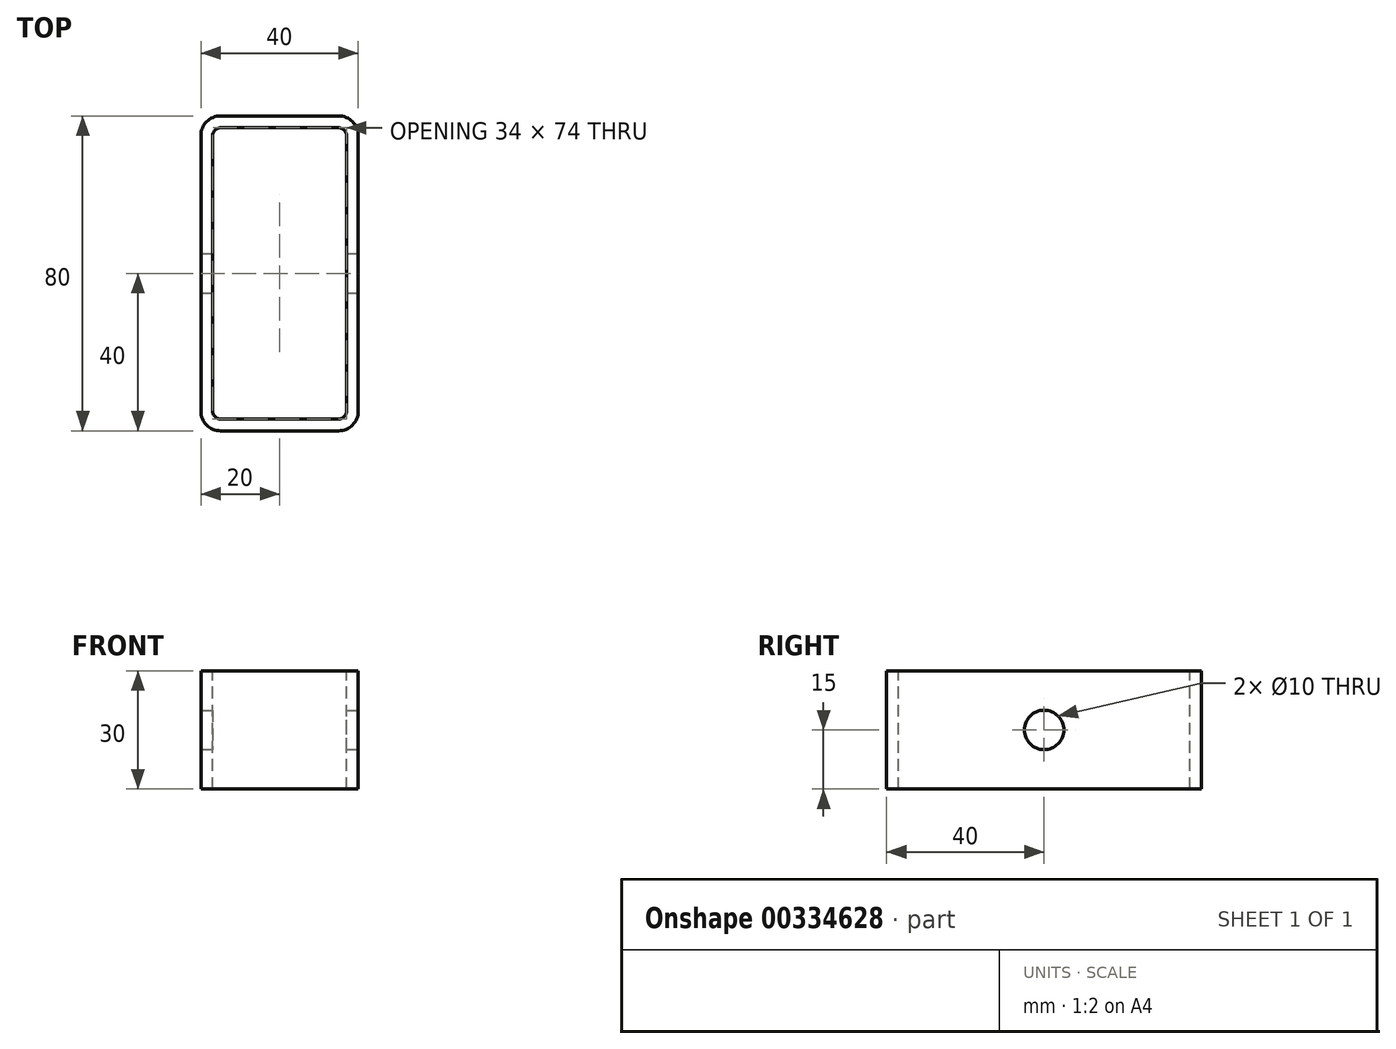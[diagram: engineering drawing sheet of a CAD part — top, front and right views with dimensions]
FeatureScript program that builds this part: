
annotation { "Feature Type Name" : "Feature", "Feature Type Description" : "" }
export const myFeature = defineFeature(function(context is Context, id is Id, definition is map)
    precondition{}
    {
        {
            var Q0;
            Q0=qCreatedBy(makeId("Top.planeOp"),FACE);
            var sketch = newSketch(context, id + "F0", { "sketchPlane" : qUnion([Q0])});
            skLineSegment(sketch, "E0.bottom", {"start": v(20, 40) * mm, "end": v(-20, 40) * mm});
            skLineSegment(sketch, "E0.top", {"start": v(20, -40) * mm, "end": v(-20, -40) * mm});
            skLineSegment(sketch, "E0.left", {"start": v(20, 40) * mm, "end": v(20, -40) * mm});
            skLineSegment(sketch, "E0.right", {"start": v(-20, 40) * mm, "end": v(-20, -40) * mm});
            skPoint(sketch, "E0.middle", {"position": v(0, 0) * mm});
            skSolve(sketch);
        }
        {
            var Q0;
            Q0=makeQuery(id+"F0.imprint","IMPRINT",FACE,{"disambiguationData":[TD([[makeQuery(id+"F0.imprint","IMPRINT",EDGE,{"derivedFrom":sQuery(id+"F0.wireOp",EDGE,"E0.bottom")}),1.0]])]});
            extrude(context, id + "F1", {"entities" : qUnion([Q0]), "depth" : 30 * mm});
        }
        {
            var Q0;
            Q0=makeQuery(id+"F1.opExtrude","SWEPT_EDGE",EDGE,{"disambiguationData":[OSD([sQuery(id+"F0.wireOp",EDGE,"E0.bottom"),sQuery(id+"F0.wireOp",EDGE,"E0.left")])]});
            var Q1;
            Q1=makeQuery(id+"F1.opExtrude","SWEPT_EDGE",EDGE,{"disambiguationData":[OSD([sQuery(id+"F0.wireOp",EDGE,"E0.bottom"),sQuery(id+"F0.wireOp",EDGE,"E0.right")])]});
            var Q2;
            Q2=makeQuery(id+"F1.opExtrude","SWEPT_EDGE",EDGE,{"disambiguationData":[OSD([sQuery(id+"F0.wireOp",EDGE,"E0.top"),sQuery(id+"F0.wireOp",EDGE,"E0.right")])]});
            var Q3;
            Q3=makeQuery(id+"F1.opExtrude","SWEPT_EDGE",EDGE,{"disambiguationData":[OSD([sQuery(id+"F0.wireOp",EDGE,"E0.top"),sQuery(id+"F0.wireOp",EDGE,"E0.left")])]});
            fillet(context, id + "F2", {"entities" : qUnion([Q0, Q1, Q2, Q3]), "radius" : 5 * mm, "tangentPropagation" : true, "allowEdgeOverflow" : false});
        }
        {
            var Q0;
            Q0=makeQuery(id+"F1.opExtrude","CAP_FACE",FACE,{"disambiguationData":[OSD([sQuery(id+"F0.wireOp",EDGE,"E0.bottom"),sQuery(id+"F0.wireOp",EDGE,"E0.top"),sQuery(id+"F0.wireOp",EDGE,"E0.left"),sQuery(id+"F0.wireOp",EDGE,"E0.right")])],"isStart":false});
            var sketch = newSketch(context, id + "F3", { "sketchPlane" : qUnion([Q0])});
            skLineSegment(sketch, "E1.0.0", {"start": v(-15, -40) * mm, "end": v(15, -40) * mm});
            skArc(sketch, "E1.0.1", {"start": v(15, -40) * mm, "mid": v(18.54, -38.54) * mm, "end": v(20, -35) * mm});
            skLineSegment(sketch, "E1.0.2", {"start": v(20, -35) * mm, "end": v(20, 35) * mm});
            skArc(sketch, "E1.0.3", {"start": v(20, 35) * mm, "mid": v(18.54, 38.54) * mm, "end": v(15, 40) * mm});
            skLineSegment(sketch, "E1.0.4", {"start": v(15, 40) * mm, "end": v(-15, 40) * mm});
            skArc(sketch, "E1.0.5", {"start": v(-15, 40) * mm, "mid": v(-18.54, 38.54) * mm, "end": v(-20, 35) * mm});
            skLineSegment(sketch, "E1.0.6", {"start": v(-20, 35) * mm, "end": v(-20, -35) * mm});
            skArc(sketch, "E1.0.7", {"start": v(-20, -35) * mm, "mid": v(-18.54, -38.54) * mm, "end": v(-15, -40) * mm});
            skLineSegment(sketch, "E2.0", {"start": v(15, 37) * mm, "end": v(-15, 37) * mm});
            skArc(sketch, "E2.1", {"start": v(17, 35) * mm, "mid": v(16.41, 36.41) * mm, "end": v(15, 37) * mm});
            skArc(sketch, "E2.2", {"start": v(-15, 37) * mm, "mid": v(-16.41, 36.41) * mm, "end": v(-17, 35) * mm});
            skLineSegment(sketch, "E2.3", {"start": v(17, -35) * mm, "end": v(17, 35) * mm});
            skLineSegment(sketch, "E2.4", {"start": v(-17, 35) * mm, "end": v(-17, -35) * mm});
            skArc(sketch, "E2.5", {"start": v(-17, -35) * mm, "mid": v(-16.41, -36.41) * mm, "end": v(-15, -37) * mm});
            skLineSegment(sketch, "E2.6", {"start": v(-15, -37) * mm, "end": v(15, -37) * mm});
            skArc(sketch, "E2.7", {"start": v(15, -37) * mm, "mid": v(16.41, -36.41) * mm, "end": v(17, -35) * mm});
            skSolve(sketch);
        }
        {
            var Q0;
            Q0=makeQuery(id+"F3.imprint","IMPRINT",FACE,{"disambiguationData":[TD([[makeQuery(id+"F3.imprint","IMPRINT",EDGE,{"derivedFrom":sQuery(id+"F3.wireOp",EDGE,"E2.0")}),1.0]])]});
            extrude(context, id + "F4", {"entities" : qUnion([Q0]), "operationType" : NewBodyOperationType.REMOVE, "oppositeDirection" : true, "depth" : 30 * mm});
        }
        {
            var Q0;
            Q0=makeQuery(id+"F1.opExtrude","SWEPT_FACE",FACE,{"disambiguationData":[OSD([sQuery(id+"F0.wireOp",EDGE,"E0.left")])]});
            var sketch = newSketch(context, id + "F5", { "sketchPlane" : qUnion([Q0])});
            skCircle(sketch, "E3", {"center": v(0, 15) * mm, "radius": 5 * mm});
            skPoint(sketch, "E3.centerSnap0", {"position": v(35, 15) * mm});
            skSolve(sketch);
        }
        {
            var Q0;
            Q0=makeQuery(id+"F5.imprint","IMPRINT",FACE,{"disambiguationData":[TD([[makeQuery(id+"F5.imprint","IMPRINT",EDGE,{"derivedFrom":sQuery(id+"F5.wireOp",EDGE,"E3")}),1.0]])]});
            extrude(context, id + "F6", {"entities" : qUnion([Q0]), "operationType" : NewBodyOperationType.REMOVE, "endBound" : BoundingType.THROUGH_ALL, "oppositeDirection" : true, "depth" : 30 * mm});
        }
    });
